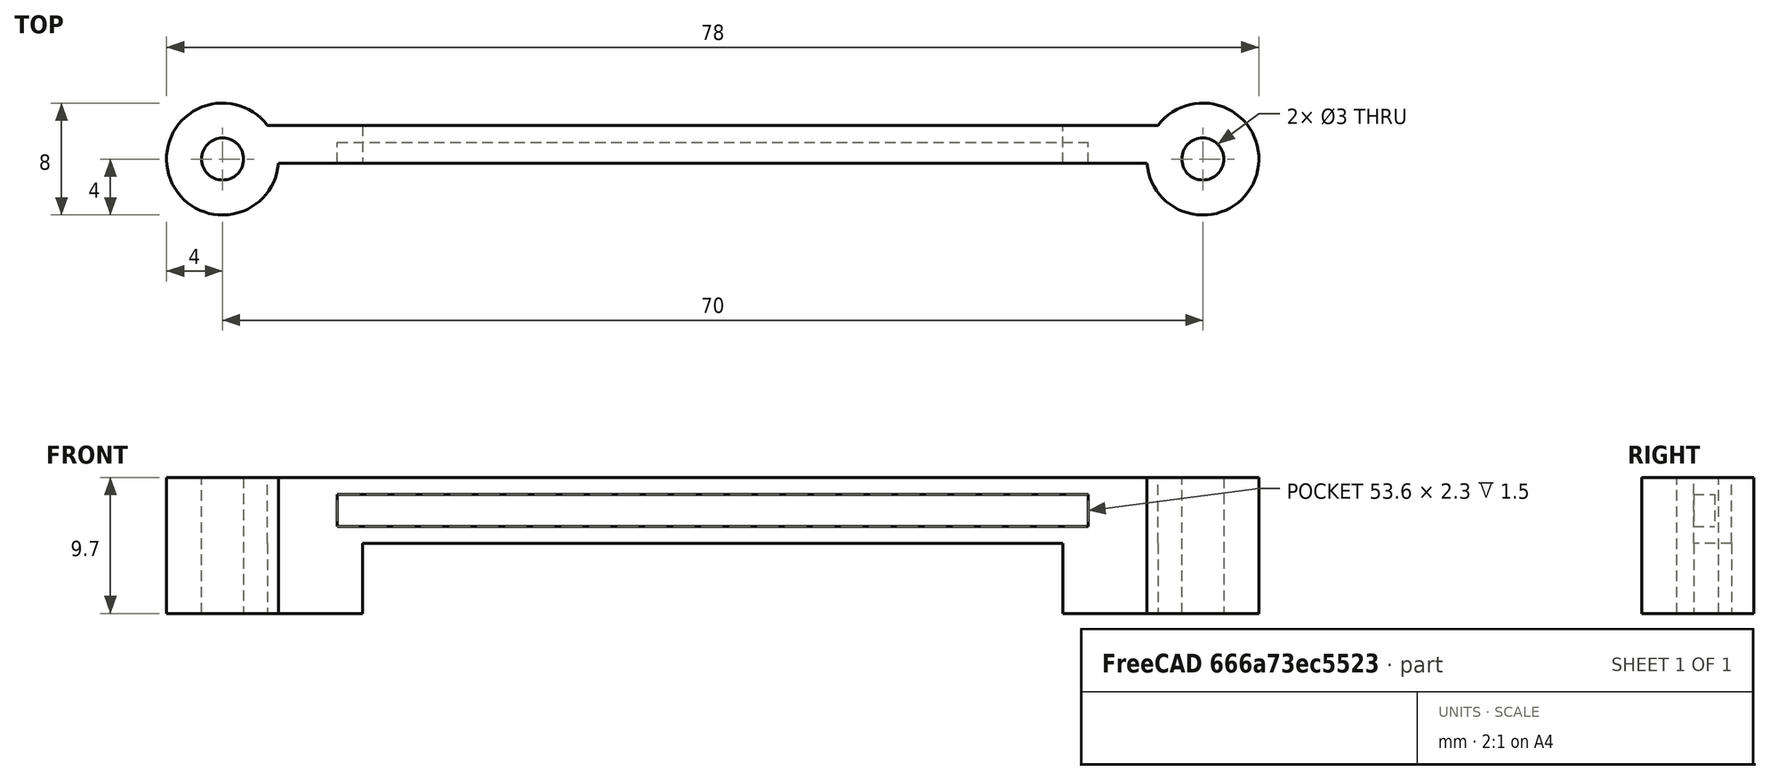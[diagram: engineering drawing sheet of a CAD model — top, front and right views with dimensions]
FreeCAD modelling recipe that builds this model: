
FCSTD DOCUMENT  (FreeCAD 0.20R29603 (Git))
Label: blackpill-fastener
License: All rights reserved
LicenseURL: http://en.wikipedia.org/wiki/All_rights_reserved
objects: Sketcher::SketchObject×6, PartDesign::Pad×3, PartDesign::Pocket×3, Spreadsheet::Sheet×1, PartDesign::Body×1, Mesh::Feature×1
note: 19 computed .brp shape members not serialized (recipe doc carries the construction recipe); baked Part::Feature solids carry a one-line shape summary decoded from their .brp

FEATURE [Sketcher::SketchObject] Sketch
  FullyConstrained = true
  MapMode = 5
  Support = -> [XY_Plane]
  expr: .Constraints.Space1 = Spreadsheet.Space
  expr: .Constraints.Space2 = Spreadsheet.Space
  expr: .Constraints.Space3 = Spreadsheet.Space
  expr: .Constraints.Thickness1 = Spreadsheet.Thickness
  expr: .Constraints.Thickness2 = Spreadsheet.Thickness
  expr: .Constraints.Thickness3 = Spreadsheet.Thickness
  expr: .Constraints.Thickness4 = Spreadsheet.Thickness
  expr: .Constraints.Thickness5 = Spreadsheet.Thickness
  expr: .Constraints.Thickness6 = Spreadsheet.Thickness
  expr: Constraints[36] = Spreadsheet.BoltPad
  expr: Constraints[37] = Spreadsheet.BoltPad
  expr: Constraints[6] = Spreadsheet.PCBLength
  sketch-geometry (21):
    g0: LineSegment StartX=-26.5 StartY=10.9 StartZ=0 EndX=26.5 EndY=10.9 EndZ=0
    g1: LineSegment StartX=26.5 StartY=10.9 StartZ=0 EndX=26.5 EndY=-10.9 EndZ=0
    g2: LineSegment StartX=26.5 StartY=-10.9 StartZ=0 EndX=-26.5 EndY=-10.9 EndZ=0
    g3: LineSegment StartX=-26.5 StartY=-10.9 StartZ=0 EndX=-26.5 EndY=10.9 EndZ=0
    g4: LineSegment StartX=-26.8 StartY=9.7 StartZ=0 EndX=-26.8 EndY=11.2 EndZ=0
    g5: LineSegment StartX=-26.8 StartY=11.2 StartZ=0 EndX=26.8 EndY=11.2 EndZ=0
    g6: LineSegment StartX=26.8 StartY=11.2 StartZ=0 EndX=26.8 EndY=9.7 EndZ=0
    g7: LineSegment StartX=-26.8 StartY=9.7 StartZ=0 EndX=26.8 EndY=9.7 EndZ=0
    g8: LineSegment StartX=-26.8 StartY=9.7 StartZ=0 EndX=-28 EndY=9.7 EndZ=0
    g9: LineSegment StartX=-28 StartY=9.7 StartZ=0 EndX=-28 EndY=12.4 EndZ=0
    g10: LineSegment StartX=26.8 StartY=9.7 StartZ=0 EndX=28 EndY=9.7 EndZ=0
    g11: LineSegment StartX=28 StartY=9.7 StartZ=0 EndX=28 EndY=12.4 EndZ=0
    g12: LineSegment StartX=-28 StartY=12.4 StartZ=0 EndX=28 EndY=12.4 EndZ=0
    g13: ArcOfCircle CenterX=-35 CenterY=10 CenterZ=0 NormalX=0 NormalY=0 NormalZ=1 AngleXU=0 Radius=4 StartAngle=0.643501 EndAngle=6.20811
    g14: ArcOfCircle CenterX=35 CenterY=10 CenterZ=0 NormalX=0 NormalY=0 NormalZ=1 AngleXU=0 Radius=4 StartAngle=3.21666 EndAngle=8.78128
    g15: GeomPoint X=-35 Y=-10 Z=0
    g16: GeomPoint X=35 Y=-10 Z=0
    g17: LineSegment StartX=-28 StartY=12.4 StartZ=0 EndX=-31.8 EndY=12.4 EndZ=0
    g18: LineSegment StartX=-28 StartY=9.7 StartZ=0 EndX=-31.0113 EndY=9.7 EndZ=0
    g19: LineSegment StartX=28 StartY=12.4 StartZ=0 EndX=31.8 EndY=12.4 EndZ=0
    g20: LineSegment StartX=28 StartY=9.7 StartZ=0 EndX=31.0113 EndY=9.7 EndZ=0
  constraints (55):
    c: Coincident(g0,g1)
    c: Coincident(g1,g2)
    c: Coincident(g2,g3)
    c: Coincident(g3,g0)
    c: Horizontal(g2)
    c: Vertical(g1)
    c: DistanceX(g0,g0) = 53
    c: DistanceY(g1,g0) = 21.8
    c: Symmetric(g0,g0,g-2)
    c: Symmetric(g0,g2,g-1)
    c: Vertical(g4)
    c: DistanceX(g4,g0) = 0.3  'Space1'
    c: DistanceY(g0,g4) = 0.3  'Space2'
    c: DistanceY(g4,g0) = 1.2  'Thickness1'
    c: Coincident(g5,g4)
    c: Horizontal(g5)
    c: DistanceX(g0,g5) = 0.3  'Space3'
    c: Coincident(g6,g5)
    c: Vertical(g6)
    c: DistanceY(g6,g0) = 1.2  'Thickness2'
    c: Coincident(g7,g4)
    c: Coincident(g7,g6)
    c: Coincident(g8,g7)
    c: Horizontal(g8)
    c: Coincident(g9,g8)
    c: Vertical(g9)
    c: DistanceX(g8,g8) = 1.2  'Thickness3'
    c: DistanceY(g4,g9) = 1.2  'Thickness4'
    c: Coincident(g10,g7)
    c: Horizontal(g10)
    c: DistanceX(g10,g10) = 1.2  'Thickness5'
    c: Coincident(g11,g10)
    c: Vertical(g11)
    c: DistanceY(g5,g11) = 1.2  'Thickness6'
    c: Coincident(g12,g9)
    c: Coincident(g12,g11)
    c: Diameter(g13) = 8
    c: Diameter(g14) = 8
    c: Symmetric(g13,g14,g-2)  'BoltCenter1'
    c: Symmetric(g15,g16,g-2)  'BoltCenter2'
    c: Symmetric(g13,g15,g-1)  'BoltCenter3'
    c: DistanceX(g13,g14) = 70  'BoltDistance1'
    c: DistanceY(g15,g13) = 20  'BoltDistance2'
    c: Coincident(g17,g9)
    c: Coincident(g17,g13)
    c: Coincident(g18,g8)
    c: Coincident(g18,g13)
    c: Horizontal(g17)
    c: Horizontal(g18)
    c: Coincident(g19,g11)
    c: Coincident(g19,g14)
    c: Coincident(g20,g10)
    c: Coincident(g20,g14)
    c: Horizontal(g19)
    c: Horizontal(g20)
FEATURE [Spreadsheet::Sheet] Spreadsheet
  cells = A1=Space; B1(Space)=0.3; A2=Thickness; B2(Thickness)=1.2; A3=Bolt Pad Diameter; B3(BoltPad)=8; A4=Bolt Diameter; B4(Bolt)=3; A5=Support Height; B5(SupportHeight)=5; A6=Support Length; B6(SupportLength)=10; A8=PCB Thickness; B8(PCBThickness)=1.7; A9=PCB Length; B9(PCBLength)=53
FEATURE [PartDesign::Pad] Pad
  Direction = (0,0,1)
  Length = 4.7
  Length2 = 10
  Profile = -> Sketch
  ReferenceAxis = -> Sketch [N_Axis]
  Type = 0
  expr: Length = 2 * Spreadsheet.Thickness + Spreadsheet.PCBThickness + 2 * Spreadsheet.Space
FEATURE [Sketcher::SketchObject] Sketch001
  ExternalGeometry = -> [Pad]
  FullyConstrained = true
  MapMode = 5
  Placement = pos=(0,0,0) rot=(1,0,0;3.14159rad)
  Support = -> [Pad]
  expr: Constraints[10] = Spreadsheet.SupportLength
  sketch-geometry (4):
    g0: LineSegment StartX=25 StartY=-9.7 StartZ=0 EndX=25 EndY=-12.4 EndZ=0
    g1: ArcOfCircle CenterX=35 CenterY=-10 CenterZ=0 NormalX=0 NormalY=0 NormalZ=1 AngleXU=0 Radius=4 StartAngle=3.78509 EndAngle=9.34971
    g2: LineSegment StartX=25 StartY=-12.4 StartZ=0 EndX=31.8 EndY=-12.4 EndZ=0
    g3: LineSegment StartX=25 StartY=-9.7 StartZ=0 EndX=31.0113 EndY=-9.7 EndZ=0
  constraints (11):
    c: Vertical(g0)
    c: Coincident(g1,g-5)
    c: Coincident(g1,g-5)
    c: Coincident(g2,g0)
    c: Coincident(g2,g1)
    c: Coincident(g3,g0)
    c: Coincident(g3,g1)
    c: Horizontal(g2)
    c: Horizontal(g3)
    c: PointOnObject(g0,g-4)
    c: DistanceX(g0,g1) = 10
FEATURE [PartDesign::Pad] Pad001  label="RightSupport"
  BaseFeature = -> Pad
  Direction = (0,0,-1)
  Length = 5
  Length2 = 10
  Profile = -> Sketch001
  ReferenceAxis = -> Sketch001 [N_Axis]
  Type = 0
  expr: Length = Spreadsheet.SupportHeight
FEATURE [Sketcher::SketchObject] Sketch002
  ExternalGeometry = -> [Pad001]
  FullyConstrained = true
  MapMode = 5
  Placement = pos=(0,0,0) rot=(1,0,0;3.14159rad)
  Support = -> [Pad001]
  expr: Constraints[10] = Spreadsheet.SupportLength
  sketch-geometry (4):
    g0: ArcOfCircle CenterX=-35 CenterY=-10 CenterZ=0 NormalX=0 NormalY=0 NormalZ=1 AngleXU=0 Radius=4 StartAngle=0.0750705 EndAngle=5.63968
    g1: LineSegment StartX=-31.0113 StartY=-9.7 StartZ=0 EndX=-25 EndY=-9.7 EndZ=0
    g2: LineSegment StartX=-31.8 StartY=-12.4 StartZ=0 EndX=-25 EndY=-12.4 EndZ=0
    g3: LineSegment StartX=-25 StartY=-12.4 StartZ=0 EndX=-25 EndY=-9.7 EndZ=0
  constraints (11):
    c: Coincident(g1,g0)
    c: Horizontal(g1)
    c: Coincident(g2,g0)
    c: Horizontal(g2)
    c: Coincident(g3,g2)
    c: Coincident(g3,g1)
    c: Vertical(g3)
    c: Coincident(g0,g-3)
    c: Coincident(g0,g-3)
    c: PointOnObject(g2,g-5)
    c: DistanceX(g0,g1) = 10
FEATURE [PartDesign::Pad] Pad002  label="LeftSupport"
  BaseFeature = -> Pad001
  Direction = (0,0,-1)
  Length = 5
  Length2 = 10
  Profile = -> Sketch002
  ReferenceAxis = -> Sketch002 [N_Axis]
  Type = 0
  expr: Length = Spreadsheet.SupportHeight
FEATURE [Sketcher::SketchObject] Sketch003
  ExternalGeometry = -> [Pad002]
  FullyConstrained = true
  MapMode = 5
  Placement = pos=(-3e-16,9.7,0) rot=(1,0,0;1.5708rad)
  Support = -> [Pad002]
  expr: Constraints[10] = Spreadsheet.PCBThickness + 2 * Spreadsheet.Space
  expr: Constraints[7] = Spreadsheet.PCBLength + 2 * Spreadsheet.Space
  expr: Constraints[9] = Spreadsheet.Thickness
  sketch-geometry (4):
    g0: LineSegment StartX=-26.8 StartY=3.5 StartZ=0 EndX=26.8 EndY=3.5 EndZ=0
    g1: LineSegment StartX=26.8 StartY=1.2 StartZ=0 EndX=26.8 EndY=3.5 EndZ=0
    g2: LineSegment StartX=-26.8 StartY=3.5 StartZ=0 EndX=-26.8 EndY=1.2 EndZ=0
    g3: LineSegment StartX=-26.8 StartY=1.2 StartZ=0 EndX=26.8 EndY=1.2 EndZ=0
  constraints (11):
    c: Coincident(g1,g0)
    c: Coincident(g2,g0)
    c: Coincident(g3,g1)
    c: Horizontal(g3)
    c: Symmetric(g0,g0,g-2)
    c: Vertical(g2)
    c: Vertical(g1)
    c: DistanceX(g0,g0) = 53.6
    c: Coincident(g3,g2)
    c: DistanceY(g0,g-3) = 1.2
    c: DistanceY(g2,g0) = 2.3
FEATURE [PartDesign::Pocket] Pocket
  BaseFeature = -> Pad002
  Direction = (0,1,-2e-16)
  Length = 1.5
  Length2 = 5
  Profile = -> Sketch003
  ReferenceAxis = -> Sketch003 [N_Axis]
  Type = 0
  expr: Length = Spreadsheet.Thickness + Spreadsheet.Space
FEATURE [Sketcher::SketchObject] Sketch004
  ExternalGeometry = -> [Pocket]
  FullyConstrained = true
  MapMode = 5
  Placement = pos=(0,0,4.7) rot=(0,0,1;0rad)
  Support = -> [Pocket]
  expr: Constraints[0] = Spreadsheet.Bolt
  sketch-geometry (1):
    g0: Circle CenterX=-35 CenterY=10 CenterZ=0 NormalX=0 NormalY=0 NormalZ=1 AngleXU=0 Radius=1.5
  constraints (2):
    c: Diameter(g0) = 3
    c: Coincident(g0,g-3)
FEATURE [PartDesign::Pocket] Pocket001  label="LeftBolt"
  BaseFeature = -> Pocket
  Direction = (0,0,-1)
  Length = 15
  Length2 = 5
  Profile = -> Sketch004
  ReferenceAxis = -> Sketch004 [N_Axis]
  Type = 0
FEATURE [Sketcher::SketchObject] Sketch005
  ExternalGeometry = -> [Pocket001]
  FullyConstrained = true
  MapMode = 5
  Placement = pos=(0,0,4.7) rot=(0,0,1;0rad)
  Support = -> [Pocket001]
  expr: Constraints[0] = Spreadsheet.Bolt
  sketch-geometry (1):
    g0: Circle CenterX=35 CenterY=10 CenterZ=0 NormalX=0 NormalY=0 NormalZ=1 AngleXU=0 Radius=1.5
  constraints (2):
    c: Diameter(g0) = 3
    c: Coincident(g0,g-3)
FEATURE [PartDesign::Pocket] Pocket002  label="RightBolt"
  BaseFeature = -> Pocket001
  Direction = (0,0,-1)
  Length = 15
  Length2 = 5
  Profile = -> Sketch005
  ReferenceAxis = -> Sketch005 [N_Axis]
  Type = 0
FEATURE [PartDesign::Body] Body
  Group = -> [Sketch,Pad,Sketch001,Pad001,Sketch002,Pad002,Sketch003,Pocket,Sketch004,Pocket001,Sketch005,Pocket002]
  Origin = -> Origin
  Tip = -> Pocket002
FEATURE [Mesh::Feature] Mesh  label="Body (Meshed)"
